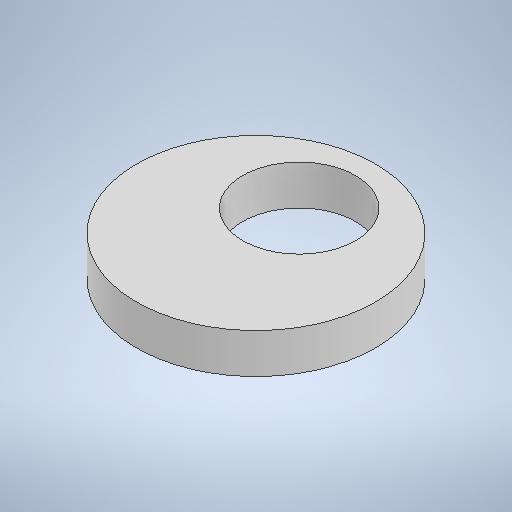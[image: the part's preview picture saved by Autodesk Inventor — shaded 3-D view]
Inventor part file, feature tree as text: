
AUTODESK INVENTOR PART (.ipt)
format: ipt  version: 2025.1 (Build 291241000, 241)  size: 227,840 bytes
history: native  units: mm
features: extrude x1, sketch x1
ambient origin geometry x8: Origin, YZ Plane, XZ Plane, XY Plane, X Axis, Y Axis, Z Axis, Center Point
bodies: Solid1 (feature_tree)
feature tree (2):
  extrude  "Extrusion1"  Depth=3.0mm
  sketch  "Sketch1"  dims[d0=18.0mm d1=8.5mm d2=3.25mm d3=3.0mm d4=0.0mm]
